# Revit family: BL4-FP Avec hôte
name_source: partatom
category: Dispositifs d'éclairage
units: mm (PartAtom-declared; Revit-internal decimal feet)

## family parameters
Conserver l'orientation des annotations = Oui
Cote de connecteur circulaire = Utiliser le diamètre
Couper avec des vides une fois chargée = Non
Hôte = Face
Partagée = Non
Point de calcul de pièce = Non
Type d'élément = Normal

## types (2) — shared parameters
Alimentation = 110-240 V AC
Charge Cos ɸ =0.5 = 500 VA
Charge Cos ɸ =1 = 1000 W
Charge LED = 200 W
Classe = II
Code d'assemblage = D5010200
Consommation = 0.30 W
Fabricant = B.E.G.
Hauteur de montage max = 350 cm
IP = 20
Image du type = 360°.jpg
Marque = LUXOMAT
Mode de pose = Faux Plafond
Relais = 4.3 A
Température ambiante = -25°C à +50°C
Type de Sortie = TOR
URL = https://www.beg-luxomat.com
zero-valued in all types: Elévation par défaut

## per-type parameters (varying)
| type | Commentaires du type | Modèle | Référence |
| BL4-FP réf 93288 | DET.MOUV.1 CONTACT.360°/Ø19M FAUX PLAFOND | BL4-FP | 93288 |
| BL4-PLUS-FP réf 93404 | DET.PRES.1 CONTACT.360°/Ø19M FAUX PLAFOND | BL4-PLUS-FP | 93404 |
